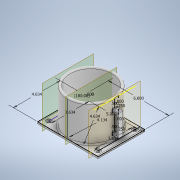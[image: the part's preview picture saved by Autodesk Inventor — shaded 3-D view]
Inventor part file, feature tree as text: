
AUTODESK INVENTOR PART (.ipt)
format: ipt  version: 2020 (Build 240168000, 168)  size: 445,440 bytes
history: native  units: in
note: dims shown in document units (in); Inventor stores cm internally (conversion verified against a paired STEP export)
features: extrude x6, sketch x4, plane x3, fillet x2, hole x1, mirror x1
ambient origin geometry x8: Origin, YZ Plane, XZ Plane, XY Plane, X Axis, Y Axis, Z Axis, Center Point
bodies: Solid1 (feature_tree)
feature tree (17):
  sketch  "Sketch1"  dims[d0=6.0in d1=4.6339in]
  extrude  "Extrusion1"  Depth=4.6339in
  extrude  "Extrusion2"  TaperAngle=180.0deg  [1 undecoded]
  hole  "Hole1"  [1 undecoded]
  extrude  "Extrusion3"  Depth=0.0625in
  plane  "Work Plane1"
  plane  "Work Plane2"
  sketch  "Sketch3"  dims[d5=5.0in d6=0.5in]
  extrude  "Extrusion4"  Depth=0.0625in
  extrude  "Extrusion5"  Depth=0.0625in
  extrude  "Extrusion6"  Depth=0.0625in TaperAngle=0.0deg
  fillet  "Fillet1"  Radius=0.1875in
  fillet  "Fillet2"  Radius=0.5in
  plane  "Work Plane3"
  mirror  "Mirror2"
  sketch  "Sketch2"  dims[d3=0.5in d4=180.0deg]
  sketch  "Sketch5"  dims[d7=3.634in d8=3.634in d9=4.1339in d10=4.6339in d11=3.5433in d12=0.0in d13=0.1875in d14=0.0in d15=0.266in d16=0.625in d17=0.507in d18=0.25in d19=0.5635in d20=1.0in d21=0.8108in d22=0.5in d23=0.5in d24=0.5in d25=0.5in d26=0.0625in d27=0.0in d28=1.0in d29=0.25in d30=0.5in d31=2.0in d32=0.25in d33=0.5in d34=0.125in d35=0.0in d36=0.375in d37=0.0in d38=0.25in d39=0.0in d40=0.0625in d41=0.125in]
note: 2 required parameter values undecoded (feature->parameter linkage not recoverable at this tier; creation-order binding heuristic only, values carry confidence <= 0.55)
